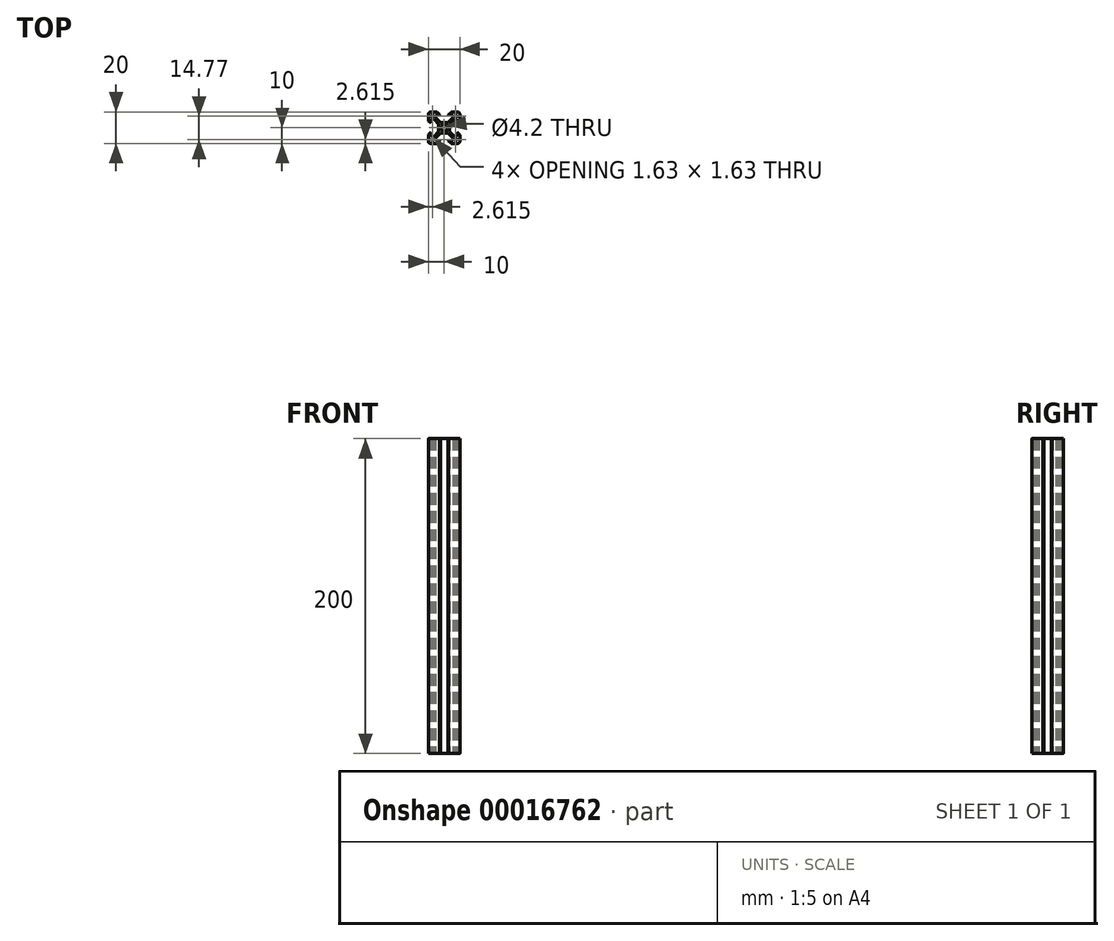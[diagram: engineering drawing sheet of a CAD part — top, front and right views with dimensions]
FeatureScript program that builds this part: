
annotation { "Feature Type Name" : "Feature", "Feature Type Description" : "" }
export const myFeature = defineFeature(function(context is Context, id is Id, definition is map)
    precondition{}
    {
        {
            var Q0;
            Q0=qCreatedBy(makeId("Top.planeOp"),FACE);
            var sketch = newSketch(context, id + "F0", { "sketchPlane" : qUnion([Q0])});
            skLineSegment(sketch, "E0", {"start": v(-8.2, -8.2) * mm, "end": v(-6.57, -8.2) * mm});
            skLineSegment(sketch, "E1", {"start": v(-8.2, -6.57) * mm, "end": v(-8.2, -8.2) * mm});
            skLineSegment(sketch, "E2", {"start": v(-7.66, -6.57) * mm, "end": v(-8.2, -6.57) * mm});
            skLineSegment(sketch, "E3", {"start": v(-6.57, -7.66) * mm, "end": v(-7.66, -6.57) * mm});
            skLineSegment(sketch, "E4", {"start": v(-6.57, -8.2) * mm, "end": v(-6.57, -7.66) * mm});
            skLineSegment(sketch, "E5", {"start": v(7.66, -6.57) * mm, "end": v(6.57, -7.66) * mm});
            skLineSegment(sketch, "E6", {"start": v(8.2, -6.57) * mm, "end": v(7.66, -6.57) * mm});
            skLineSegment(sketch, "E7", {"start": v(8.2, -8.2) * mm, "end": v(8.2, -6.57) * mm});
            skLineSegment(sketch, "E8", {"start": v(6.57, -8.2) * mm, "end": v(8.2, -8.2) * mm});
            skLineSegment(sketch, "E9", {"start": v(6.57, -7.66) * mm, "end": v(6.57, -8.2) * mm});
            skCircle(sketch, "E10", {"center": v(0, 0) * mm, "radius": 2.1 * mm});
            skLineSegment(sketch, "E11", {"start": v(8.2, 8.2) * mm, "end": v(6.57, 8.2) * mm});
            skLineSegment(sketch, "E12", {"start": v(8.2, 6.57) * mm, "end": v(8.2, 8.2) * mm});
            skLineSegment(sketch, "E13", {"start": v(7.66, 6.57) * mm, "end": v(8.2, 6.57) * mm});
            skLineSegment(sketch, "E14", {"start": v(6.57, 7.66) * mm, "end": v(7.66, 6.57) * mm});
            skLineSegment(sketch, "E15", {"start": v(6.57, 8.2) * mm, "end": v(6.57, 7.66) * mm});
            skLineSegment(sketch, "E16", {"start": v(-7.66, 6.57) * mm, "end": v(-6.57, 7.66) * mm});
            skLineSegment(sketch, "E17", {"start": v(-8.2, 6.57) * mm, "end": v(-7.66, 6.57) * mm});
            skLineSegment(sketch, "E18", {"start": v(-8.2, 8.2) * mm, "end": v(-8.2, 6.57) * mm});
            skLineSegment(sketch, "E19", {"start": v(-6.57, 8.2) * mm, "end": v(-8.2, 8.2) * mm});
            skLineSegment(sketch, "E20", {"start": v(-6.57, 7.66) * mm, "end": v(-6.57, 8.2) * mm});
            skLineSegment(sketch, "E21", {"start": v(-6.56, 5.5) * mm, "end": v(-3.4, 2.34) * mm});
            skLineSegment(sketch, "E22", {"start": v(-3.4, 2.34) * mm, "end": v(-3.4, -2.34) * mm});
            skLineSegment(sketch, "E23", {"start": v(-3.4, -2.34) * mm, "end": v(-6.56, -5.5) * mm});
            skLineSegment(sketch, "E24", {"start": v(-6.56, -5.5) * mm, "end": v(-8.2, -5.5) * mm});
            skLineSegment(sketch, "E25", {"start": v(-8.2, -5.5) * mm, "end": v(-8.2, -2.9) * mm});
            skLineSegment(sketch, "E26", {"start": v(-8.2, -2.9) * mm, "end": v(-8.31, -2.9) * mm});
            skLineSegment(sketch, "E27", {"start": v(-8.31, -2.9) * mm, "end": v(-9.77, -4.35) * mm});
            skArc(sketch, "E28", {"start": v(-9.77, -4.35) * mm, "mid": v(-9.94, -4.6) * mm, "end": v(-10, -4.9) * mm});
            skLineSegment(sketch, "E29", {"start": v(-10, -4.9) * mm, "end": v(-10, -8.5) * mm});
            skArc(sketch, "E30", {"start": v(-10, -8.5) * mm, "mid": v(-9.56, -9.56) * mm, "end": v(-8.5, -10) * mm});
            skLineSegment(sketch, "E31", {"start": v(-8.5, -10) * mm, "end": v(-4.9, -10) * mm});
            skArc(sketch, "E32", {"start": v(-4.9, -10) * mm, "mid": v(-4.6, -9.94) * mm, "end": v(-4.35, -9.77) * mm});
            skLineSegment(sketch, "E33", {"start": v(-4.35, -9.77) * mm, "end": v(-2.9, -8.31) * mm});
            skLineSegment(sketch, "E34", {"start": v(-2.9, -8.31) * mm, "end": v(-2.9, -8.2) * mm});
            skLineSegment(sketch, "E35", {"start": v(-2.9, -8.2) * mm, "end": v(-5.5, -8.2) * mm});
            skLineSegment(sketch, "E36", {"start": v(-5.5, -8.2) * mm, "end": v(-5.5, -6.56) * mm});
            skLineSegment(sketch, "E37", {"start": v(-5.5, -6.56) * mm, "end": v(-2.34, -3.4) * mm});
            skLineSegment(sketch, "E38", {"start": v(-2.34, -3.4) * mm, "end": v(2.34, -3.4) * mm});
            skLineSegment(sketch, "E39", {"start": v(2.34, -3.4) * mm, "end": v(5.5, -6.56) * mm});
            skLineSegment(sketch, "E40", {"start": v(5.5, -6.56) * mm, "end": v(5.5, -8.2) * mm});
            skLineSegment(sketch, "E41", {"start": v(5.5, -8.2) * mm, "end": v(2.9, -8.2) * mm});
            skLineSegment(sketch, "E42", {"start": v(2.9, -8.2) * mm, "end": v(2.9, -8.31) * mm});
            skLineSegment(sketch, "E43", {"start": v(2.9, -8.31) * mm, "end": v(4.35, -9.77) * mm});
            skArc(sketch, "E44", {"start": v(4.35, -9.77) * mm, "mid": v(4.6, -9.94) * mm, "end": v(4.9, -10) * mm});
            skLineSegment(sketch, "E45", {"start": v(4.9, -10) * mm, "end": v(8.5, -10) * mm});
            skArc(sketch, "E46", {"start": v(8.5, -10) * mm, "mid": v(9.56, -9.56) * mm, "end": v(10, -8.5) * mm});
            skLineSegment(sketch, "E47", {"start": v(10, -8.5) * mm, "end": v(10, -4.9) * mm});
            skArc(sketch, "E48", {"start": v(10, -4.9) * mm, "mid": v(9.94, -4.6) * mm, "end": v(9.77, -4.35) * mm});
            skLineSegment(sketch, "E49", {"start": v(9.77, -4.35) * mm, "end": v(8.31, -2.9) * mm});
            skLineSegment(sketch, "E50", {"start": v(8.31, -2.9) * mm, "end": v(8.2, -2.9) * mm});
            skLineSegment(sketch, "E51", {"start": v(8.2, -2.9) * mm, "end": v(8.2, -5.5) * mm});
            skLineSegment(sketch, "E52", {"start": v(8.2, -5.5) * mm, "end": v(6.56, -5.5) * mm});
            skLineSegment(sketch, "E53", {"start": v(6.56, -5.5) * mm, "end": v(3.4, -2.34) * mm});
            skLineSegment(sketch, "E54", {"start": v(3.4, -2.34) * mm, "end": v(3.4, 2.34) * mm});
            skLineSegment(sketch, "E55", {"start": v(3.4, 2.34) * mm, "end": v(6.56, 5.5) * mm});
            skLineSegment(sketch, "E56", {"start": v(6.56, 5.5) * mm, "end": v(8.2, 5.5) * mm});
            skLineSegment(sketch, "E57", {"start": v(8.2, 5.5) * mm, "end": v(8.2, 2.9) * mm});
            skLineSegment(sketch, "E58", {"start": v(8.2, 2.9) * mm, "end": v(8.31, 2.9) * mm});
            skLineSegment(sketch, "E59", {"start": v(8.31, 2.9) * mm, "end": v(9.77, 4.35) * mm});
            skArc(sketch, "E60", {"start": v(9.77, 4.35) * mm, "mid": v(9.94, 4.6) * mm, "end": v(10, 4.9) * mm});
            skLineSegment(sketch, "E61", {"start": v(10, 4.9) * mm, "end": v(10, 8.5) * mm});
            skArc(sketch, "E62", {"start": v(10, 8.5) * mm, "mid": v(9.56, 9.56) * mm, "end": v(8.5, 10) * mm});
            skLineSegment(sketch, "E63", {"start": v(8.5, 10) * mm, "end": v(4.9, 10) * mm});
            skArc(sketch, "E64", {"start": v(4.9, 10) * mm, "mid": v(4.6, 9.94) * mm, "end": v(4.35, 9.77) * mm});
            skLineSegment(sketch, "E65", {"start": v(4.35, 9.77) * mm, "end": v(2.9, 8.31) * mm});
            skLineSegment(sketch, "E66", {"start": v(2.9, 8.31) * mm, "end": v(2.9, 8.2) * mm});
            skLineSegment(sketch, "E67", {"start": v(2.9, 8.2) * mm, "end": v(5.5, 8.2) * mm});
            skLineSegment(sketch, "E68", {"start": v(5.5, 8.2) * mm, "end": v(5.5, 6.56) * mm});
            skLineSegment(sketch, "E69", {"start": v(5.5, 6.56) * mm, "end": v(2.34, 3.4) * mm});
            skLineSegment(sketch, "E70", {"start": v(2.34, 3.4) * mm, "end": v(-2.34, 3.4) * mm});
            skLineSegment(sketch, "E71", {"start": v(-2.34, 3.4) * mm, "end": v(-5.5, 6.56) * mm});
            skLineSegment(sketch, "E72", {"start": v(-5.5, 6.56) * mm, "end": v(-5.5, 8.2) * mm});
            skLineSegment(sketch, "E73", {"start": v(-5.5, 8.2) * mm, "end": v(-2.9, 8.2) * mm});
            skLineSegment(sketch, "E74", {"start": v(-2.9, 8.2) * mm, "end": v(-2.9, 8.31) * mm});
            skLineSegment(sketch, "E75", {"start": v(-2.9, 8.31) * mm, "end": v(-4.35, 9.77) * mm});
            skArc(sketch, "E76", {"start": v(-4.35, 9.77) * mm, "mid": v(-4.6, 9.94) * mm, "end": v(-4.9, 10) * mm});
            skLineSegment(sketch, "E77", {"start": v(-4.9, 10) * mm, "end": v(-8.5, 10) * mm});
            skArc(sketch, "E78", {"start": v(-8.5, 10) * mm, "mid": v(-9.56, 9.56) * mm, "end": v(-10, 8.5) * mm});
            skLineSegment(sketch, "E79", {"start": v(-10, 8.5) * mm, "end": v(-10, 4.9) * mm});
            skArc(sketch, "E80", {"start": v(-10, 4.9) * mm, "mid": v(-9.94, 4.6) * mm, "end": v(-9.77, 4.35) * mm});
            skLineSegment(sketch, "E81", {"start": v(-9.77, 4.35) * mm, "end": v(-8.31, 2.9) * mm});
            skLineSegment(sketch, "E82", {"start": v(-8.31, 2.9) * mm, "end": v(-8.2, 2.9) * mm});
            skLineSegment(sketch, "E83", {"start": v(-8.2, 2.9) * mm, "end": v(-8.2, 5.5) * mm});
            skLineSegment(sketch, "E84", {"start": v(-8.2, 5.5) * mm, "end": v(-6.56, 5.5) * mm});
            skSolve(sketch);
        }
        {
            var Q0;
            Q0 = qSketchRegion(id + "F0", true);
            extrude(context, id + "F1", {"entities" : qUnion([Q0]), "depth" : 200 * mm});
        }
    });
